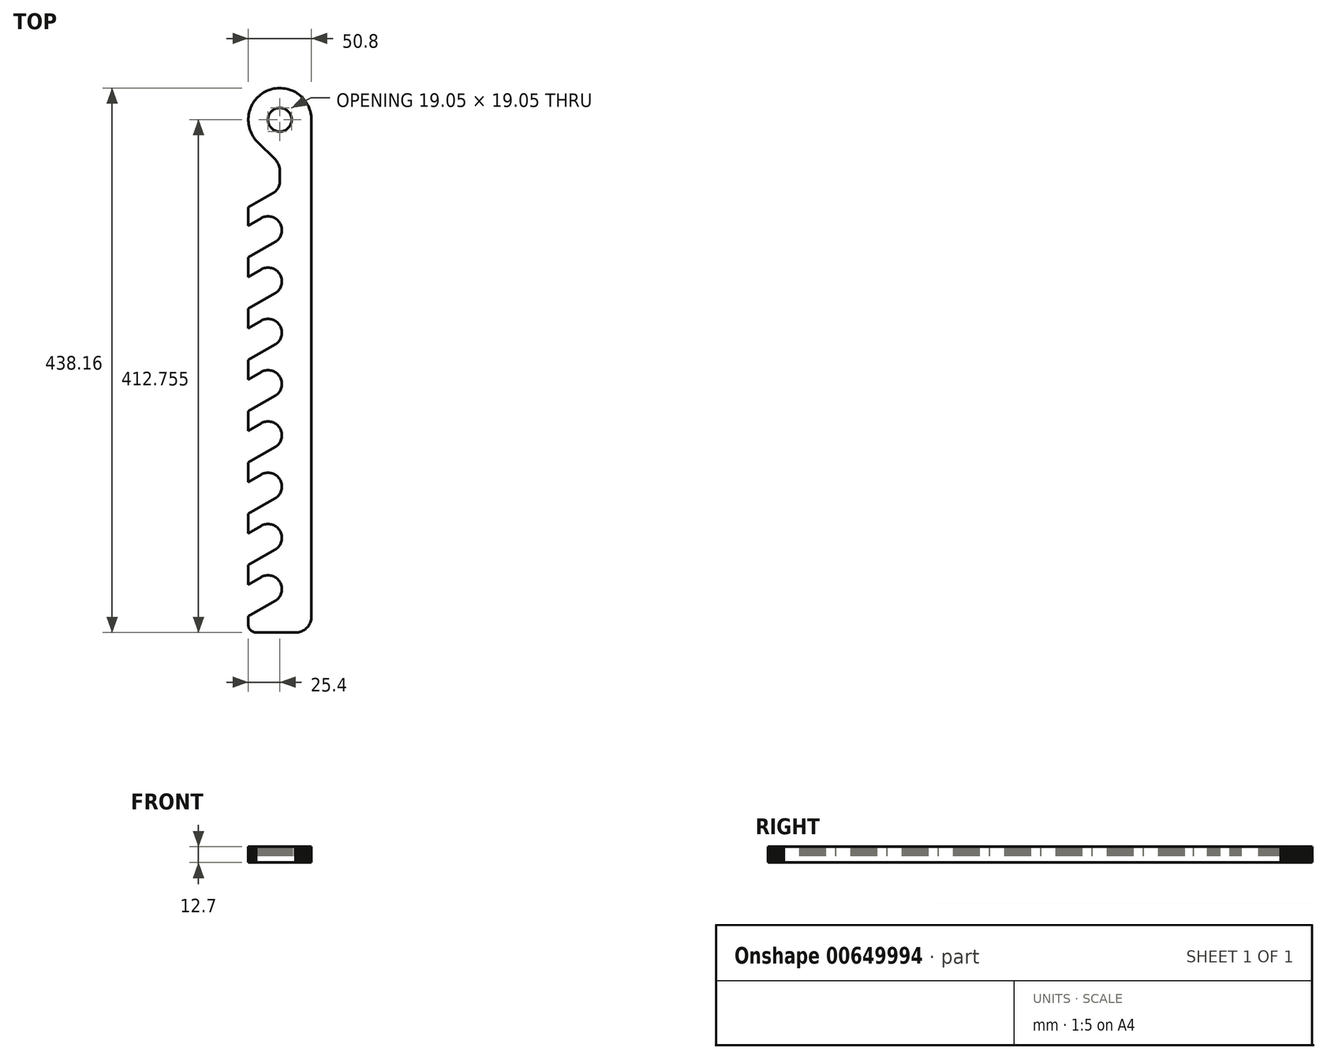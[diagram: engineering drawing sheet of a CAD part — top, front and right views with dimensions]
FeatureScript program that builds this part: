
annotation { "Feature Type Name" : "Feature", "Feature Type Description" : "" }
export const myFeature = defineFeature(function(context is Context, id is Id, definition is map)
    precondition{}
    {
        {
            var Q0;
            Q0=qCreatedBy(makeId("Top.planeOp"),FACE);
            var sketch = newSketch(context, id + "F0", { "sketchPlane" : qUnion([Q0])});
            skLineSegment(sketch, "E0", {"start": v(-25.4, -212.73) * mm, "end": v(-25.36, -213.42) * mm});
            skLineSegment(sketch, "E1", {"start": v(-25.36, -213.42) * mm, "end": v(-25.23, -214.14) * mm});
            skLineSegment(sketch, "E2", {"start": v(-25.23, -214.14) * mm, "end": v(-25.04, -214.82) * mm});
            skLineSegment(sketch, "E3", {"start": v(-25.04, -214.82) * mm, "end": v(-24.77, -215.48) * mm});
            skLineSegment(sketch, "E4", {"start": v(-24.77, -215.48) * mm, "end": v(-24.43, -216.11) * mm});
            skLineSegment(sketch, "E5", {"start": v(-24.43, -216.11) * mm, "end": v(-24.02, -216.68) * mm});
            skLineSegment(sketch, "E6", {"start": v(-24.02, -216.68) * mm, "end": v(-23.54, -217.21) * mm});
            skLineSegment(sketch, "E7", {"start": v(-23.54, -217.21) * mm, "end": v(-23, -217.68) * mm});
            skLineSegment(sketch, "E8", {"start": v(-23, -217.68) * mm, "end": v(-22.44, -218.1) * mm});
            skLineSegment(sketch, "E9", {"start": v(-22.44, -218.1) * mm, "end": v(-21.8, -218.44) * mm});
            skLineSegment(sketch, "E10", {"start": v(-21.8, -218.44) * mm, "end": v(-21.15, -218.72) * mm});
            skLineSegment(sketch, "E11", {"start": v(-21.15, -218.72) * mm, "end": v(-20.47, -218.9) * mm});
            skLineSegment(sketch, "E12", {"start": v(-20.47, -218.9) * mm, "end": v(-19.77, -219.03) * mm});
            skLineSegment(sketch, "E13", {"start": v(-19.77, -219.03) * mm, "end": v(-19.05, -219.08) * mm});
            skLineSegment(sketch, "E14", {"start": v(-19.05, -219.08) * mm, "end": v(12.7, -219.08) * mm});
            skLineSegment(sketch, "E15", {"start": v(12.7, -219.08) * mm, "end": v(13.76, -219.03) * mm});
            skLineSegment(sketch, "E16", {"start": v(13.76, -219.03) * mm, "end": v(14.8, -218.9) * mm});
            skLineSegment(sketch, "E17", {"start": v(14.8, -218.9) * mm, "end": v(15.81, -218.7) * mm});
            skLineSegment(sketch, "E18", {"start": v(15.81, -218.7) * mm, "end": v(16.83, -218.38) * mm});
            skLineSegment(sketch, "E19", {"start": v(16.83, -218.38) * mm, "end": v(17.8, -218) * mm});
            skLineSegment(sketch, "E20", {"start": v(17.8, -218) * mm, "end": v(18.75, -217.55) * mm});
            skLineSegment(sketch, "E21", {"start": v(18.75, -217.55) * mm, "end": v(19.64, -217) * mm});
            skLineSegment(sketch, "E22", {"start": v(19.64, -217) * mm, "end": v(20.51, -216.39) * mm});
            skLineSegment(sketch, "E23", {"start": v(20.51, -216.39) * mm, "end": v(21.3, -215.7) * mm});
            skLineSegment(sketch, "E24", {"start": v(21.3, -215.7) * mm, "end": v(22.03, -214.97) * mm});
            skLineSegment(sketch, "E25", {"start": v(22.03, -214.97) * mm, "end": v(22.73, -214.16) * mm});
            skLineSegment(sketch, "E26", {"start": v(22.73, -214.16) * mm, "end": v(23.33, -213.32) * mm});
            skLineSegment(sketch, "E27", {"start": v(23.33, -213.32) * mm, "end": v(23.88, -212.4) * mm});
            skLineSegment(sketch, "E28", {"start": v(23.88, -212.4) * mm, "end": v(24.32, -211.48) * mm});
            skLineSegment(sketch, "E29", {"start": v(24.32, -211.48) * mm, "end": v(24.72, -210.5) * mm});
            skLineSegment(sketch, "E30", {"start": v(24.72, -210.5) * mm, "end": v(25.02, -209.49) * mm});
            skLineSegment(sketch, "E31", {"start": v(25.02, -209.49) * mm, "end": v(25.23, -208.47) * mm});
            skLineSegment(sketch, "E32", {"start": v(25.23, -208.47) * mm, "end": v(25.36, -207.41) * mm});
            skLineSegment(sketch, "E33", {"start": v(25.36, -207.41) * mm, "end": v(25.4, -206.38) * mm});
            skLineSegment(sketch, "E34", {"start": v(0, 184.15) * mm, "end": v(0.89, 184.2) * mm});
            skLineSegment(sketch, "E35", {"start": v(0.89, 184.2) * mm, "end": v(1.76, 184.32) * mm});
            skLineSegment(sketch, "E36", {"start": v(1.76, 184.32) * mm, "end": v(2.6, 184.5) * mm});
            skLineSegment(sketch, "E37", {"start": v(2.6, 184.5) * mm, "end": v(3.45, 184.78) * mm});
            skLineSegment(sketch, "E38", {"start": v(3.45, 184.78) * mm, "end": v(4.25, 185.14) * mm});
            skLineSegment(sketch, "E39", {"start": v(4.25, 185.14) * mm, "end": v(5.02, 185.59) * mm});
            skLineSegment(sketch, "E40", {"start": v(5.02, 185.59) * mm, "end": v(5.74, 186.08) * mm});
            skLineSegment(sketch, "E41", {"start": v(5.74, 186.08) * mm, "end": v(6.41, 186.65) * mm});
            skLineSegment(sketch, "E42", {"start": v(6.41, 186.65) * mm, "end": v(7.05, 187.26) * mm});
            skLineSegment(sketch, "E43", {"start": v(7.05, 187.26) * mm, "end": v(7.6, 187.94) * mm});
            skLineSegment(sketch, "E44", {"start": v(7.6, 187.94) * mm, "end": v(8.1, 188.66) * mm});
            skLineSegment(sketch, "E45", {"start": v(8.1, 188.66) * mm, "end": v(8.53, 189.44) * mm});
            skLineSegment(sketch, "E46", {"start": v(8.53, 189.44) * mm, "end": v(8.89, 190.25) * mm});
            skLineSegment(sketch, "E47", {"start": v(8.89, 190.25) * mm, "end": v(9.17, 191.07) * mm});
            skLineSegment(sketch, "E48", {"start": v(9.17, 191.07) * mm, "end": v(9.36, 191.92) * mm});
            skLineSegment(sketch, "E49", {"start": v(9.36, 191.92) * mm, "end": v(9.48, 192.8) * mm});
            skLineSegment(sketch, "E50", {"start": v(9.48, 192.8) * mm, "end": v(9.53, 193.68) * mm});
            skLineSegment(sketch, "E51", {"start": v(9.53, 193.68) * mm, "end": v(9.48, 194.56) * mm});
            skLineSegment(sketch, "E52", {"start": v(9.48, 194.56) * mm, "end": v(9.36, 195.43) * mm});
            skLineSegment(sketch, "E53", {"start": v(9.36, 195.43) * mm, "end": v(9.17, 196.28) * mm});
            skLineSegment(sketch, "E54", {"start": v(9.17, 196.28) * mm, "end": v(8.89, 197.13) * mm});
            skLineSegment(sketch, "E55", {"start": v(8.89, 197.13) * mm, "end": v(8.53, 197.93) * mm});
            skLineSegment(sketch, "E56", {"start": v(8.53, 197.93) * mm, "end": v(8.1, 198.7) * mm});
            skLineSegment(sketch, "E57", {"start": v(8.1, 198.7) * mm, "end": v(7.6, 199.41) * mm});
            skLineSegment(sketch, "E58", {"start": v(7.6, 199.41) * mm, "end": v(7.05, 200.09) * mm});
            skLineSegment(sketch, "E59", {"start": v(7.05, 200.09) * mm, "end": v(6.41, 200.72) * mm});
            skLineSegment(sketch, "E60", {"start": v(6.41, 200.72) * mm, "end": v(5.74, 201.27) * mm});
            skLineSegment(sketch, "E61", {"start": v(5.74, 201.27) * mm, "end": v(5.02, 201.78) * mm});
            skLineSegment(sketch, "E62", {"start": v(5.02, 201.78) * mm, "end": v(4.25, 202.2) * mm});
            skLineSegment(sketch, "E63", {"start": v(4.25, 202.2) * mm, "end": v(3.45, 202.57) * mm});
            skLineSegment(sketch, "E64", {"start": v(3.45, 202.57) * mm, "end": v(2.6, 202.84) * mm});
            skLineSegment(sketch, "E65", {"start": v(2.6, 202.84) * mm, "end": v(1.76, 203.03) * mm});
            skLineSegment(sketch, "E66", {"start": v(1.76, 203.03) * mm, "end": v(0.89, 203.16) * mm});
            skLineSegment(sketch, "E67", {"start": v(0.89, 203.16) * mm, "end": v(0, 203.2) * mm});
            skLineSegment(sketch, "E68", {"start": v(0, 203.2) * mm, "end": v(-0.87, 203.16) * mm});
            skLineSegment(sketch, "E69", {"start": v(-0.87, 203.16) * mm, "end": v(-1.76, 203.03) * mm});
            skLineSegment(sketch, "E70", {"start": v(-1.76, 203.03) * mm, "end": v(-2.6, 202.84) * mm});
            skLineSegment(sketch, "E71", {"start": v(-2.6, 202.84) * mm, "end": v(-3.45, 202.57) * mm});
            skLineSegment(sketch, "E72", {"start": v(-3.45, 202.57) * mm, "end": v(-4.25, 202.2) * mm});
            skLineSegment(sketch, "E73", {"start": v(-4.25, 202.2) * mm, "end": v(-5.02, 201.78) * mm});
            skLineSegment(sketch, "E74", {"start": v(-5.02, 201.78) * mm, "end": v(-5.74, 201.27) * mm});
            skLineSegment(sketch, "E75", {"start": v(-5.74, 201.27) * mm, "end": v(-6.41, 200.72) * mm});
            skLineSegment(sketch, "E76", {"start": v(-6.41, 200.72) * mm, "end": v(-7.05, 200.09) * mm});
            skLineSegment(sketch, "E77", {"start": v(-7.05, 200.09) * mm, "end": v(-7.6, 199.41) * mm});
            skLineSegment(sketch, "E78", {"start": v(-7.6, 199.41) * mm, "end": v(-8.1, 198.7) * mm});
            skLineSegment(sketch, "E79", {"start": v(-8.1, 198.7) * mm, "end": v(-8.53, 197.93) * mm});
            skLineSegment(sketch, "E80", {"start": v(-8.53, 197.93) * mm, "end": v(-8.9, 197.13) * mm});
            skLineSegment(sketch, "E81", {"start": v(-8.9, 197.13) * mm, "end": v(-9.17, 196.28) * mm});
            skLineSegment(sketch, "E82", {"start": v(-9.17, 196.28) * mm, "end": v(-9.36, 195.43) * mm});
            skLineSegment(sketch, "E83", {"start": v(-9.36, 195.43) * mm, "end": v(-9.48, 194.56) * mm});
            skLineSegment(sketch, "E84", {"start": v(-9.48, 194.56) * mm, "end": v(-9.53, 193.68) * mm});
            skLineSegment(sketch, "E85", {"start": v(-9.53, 193.68) * mm, "end": v(-9.48, 192.8) * mm});
            skLineSegment(sketch, "E86", {"start": v(-9.48, 192.8) * mm, "end": v(-9.36, 191.92) * mm});
            skLineSegment(sketch, "E87", {"start": v(-9.36, 191.92) * mm, "end": v(-9.17, 191.07) * mm});
            skLineSegment(sketch, "E88", {"start": v(-9.17, 191.07) * mm, "end": v(-8.9, 190.25) * mm});
            skLineSegment(sketch, "E89", {"start": v(-8.9, 190.25) * mm, "end": v(-8.53, 189.44) * mm});
            skLineSegment(sketch, "E90", {"start": v(-8.53, 189.44) * mm, "end": v(-8.1, 188.66) * mm});
            skLineSegment(sketch, "E91", {"start": v(-8.1, 188.66) * mm, "end": v(-7.6, 187.94) * mm});
            skLineSegment(sketch, "E92", {"start": v(-7.6, 187.94) * mm, "end": v(-7.05, 187.26) * mm});
            skLineSegment(sketch, "E93", {"start": v(-7.05, 187.26) * mm, "end": v(-6.41, 186.65) * mm});
            skLineSegment(sketch, "E94", {"start": v(-6.41, 186.65) * mm, "end": v(-5.74, 186.08) * mm});
            skLineSegment(sketch, "E95", {"start": v(-5.74, 186.08) * mm, "end": v(-5.02, 185.59) * mm});
            skLineSegment(sketch, "E96", {"start": v(-5.02, 185.59) * mm, "end": v(-4.25, 185.14) * mm});
            skLineSegment(sketch, "E97", {"start": v(-4.25, 185.14) * mm, "end": v(-3.45, 184.78) * mm});
            skLineSegment(sketch, "E98", {"start": v(-3.45, 184.78) * mm, "end": v(-2.6, 184.5) * mm});
            skLineSegment(sketch, "E99", {"start": v(-2.6, 184.5) * mm, "end": v(-1.76, 184.32) * mm});
            skLineSegment(sketch, "E100", {"start": v(-1.76, 184.32) * mm, "end": v(-0.87, 184.2) * mm});
            skLineSegment(sketch, "E101", {"start": v(-0.87, 184.2) * mm, "end": v(0, 184.15) * mm});
            skLineSegment(sketch, "E102", {"start": v(-25.4, 123.1) * mm, "end": v(-5.55, 134.58) * mm});
            skLineSegment(sketch, "E103", {"start": v(-5.55, 134.58) * mm, "end": v(-4.74, 135.09) * mm});
            skLineSegment(sketch, "E104", {"start": v(-4.74, 135.09) * mm, "end": v(-3.98, 135.68) * mm});
            skLineSegment(sketch, "E105", {"start": v(-3.98, 135.68) * mm, "end": v(-3.26, 136.33) * mm});
            skLineSegment(sketch, "E106", {"start": v(-3.26, 136.33) * mm, "end": v(-2.6, 137.05) * mm});
            skLineSegment(sketch, "E107", {"start": v(-2.6, 137.05) * mm, "end": v(-2.01, 137.82) * mm});
            skLineSegment(sketch, "E108", {"start": v(-2.01, 137.82) * mm, "end": v(-1.48, 138.64) * mm});
            skLineSegment(sketch, "E109", {"start": v(-1.48, 138.64) * mm, "end": v(-1.04, 139.49) * mm});
            skLineSegment(sketch, "E110", {"start": v(-1.04, 139.49) * mm, "end": v(-0.68, 140.4) * mm});
            skLineSegment(sketch, "E111", {"start": v(-0.68, 140.4) * mm, "end": v(-0.38, 141.3) * mm});
            skLineSegment(sketch, "E112", {"start": v(-0.38, 141.3) * mm, "end": v(-0.17, 142.26) * mm});
            skLineSegment(sketch, "E113", {"start": v(-0.17, 142.26) * mm, "end": v(-0.04, 143.21) * mm});
            skLineSegment(sketch, "E114", {"start": v(-0.04, 143.21) * mm, "end": v(0, 144.19) * mm});
            skLineSegment(sketch, "E115", {"start": v(-3.96, 95.14) * mm, "end": v(-3.15, 95.67) * mm});
            skLineSegment(sketch, "E116", {"start": v(-3.15, 95.67) * mm, "end": v(-2.4, 96.27) * mm});
            skLineSegment(sketch, "E117", {"start": v(-2.4, 96.27) * mm, "end": v(-1.67, 96.92) * mm});
            skLineSegment(sketch, "E118", {"start": v(-1.67, 96.92) * mm, "end": v(-1.02, 97.64) * mm});
            skLineSegment(sketch, "E119", {"start": v(-1.02, 97.64) * mm, "end": v(-0.42, 98.4) * mm});
            skLineSegment(sketch, "E120", {"start": v(-0.42, 98.4) * mm, "end": v(0.1, 99.23) * mm});
            skLineSegment(sketch, "E121", {"start": v(0.1, 99.23) * mm, "end": v(0.55, 100.08) * mm});
            skLineSegment(sketch, "E122", {"start": v(0.55, 100.08) * mm, "end": v(0.91, 100.99) * mm});
            skLineSegment(sketch, "E123", {"start": v(0.91, 100.99) * mm, "end": v(1.2, 101.9) * mm});
            skLineSegment(sketch, "E124", {"start": v(1.2, 101.9) * mm, "end": v(1.42, 102.85) * mm});
            skLineSegment(sketch, "E125", {"start": v(1.42, 102.85) * mm, "end": v(1.55, 103.8) * mm});
            skLineSegment(sketch, "E126", {"start": v(1.55, 103.8) * mm, "end": v(1.59, 104.77) * mm});
            skLineSegment(sketch, "E127", {"start": v(1.59, 104.77) * mm, "end": v(1.55, 105.75) * mm});
            skLineSegment(sketch, "E128", {"start": v(1.55, 105.75) * mm, "end": v(1.42, 106.7) * mm});
            skLineSegment(sketch, "E129", {"start": v(1.42, 106.7) * mm, "end": v(1.2, 107.65) * mm});
            skLineSegment(sketch, "E130", {"start": v(1.2, 107.65) * mm, "end": v(0.91, 108.58) * mm});
            skLineSegment(sketch, "E131", {"start": v(0.91, 108.58) * mm, "end": v(0.55, 109.47) * mm});
            skLineSegment(sketch, "E132", {"start": v(0.55, 109.47) * mm, "end": v(0.1, 110.34) * mm});
            skLineSegment(sketch, "E133", {"start": v(0.1, 110.34) * mm, "end": v(-0.42, 111.15) * mm});
            skLineSegment(sketch, "E134", {"start": v(-0.42, 111.15) * mm, "end": v(-1.02, 111.93) * mm});
            skLineSegment(sketch, "E135", {"start": v(-1.02, 111.93) * mm, "end": v(-1.67, 112.63) * mm});
            skLineSegment(sketch, "E136", {"start": v(-1.67, 112.63) * mm, "end": v(-2.4, 113.28) * mm});
            skLineSegment(sketch, "E137", {"start": v(-2.4, 113.28) * mm, "end": v(-3.15, 113.88) * mm});
            skLineSegment(sketch, "E138", {"start": v(-3.15, 113.88) * mm, "end": v(-3.96, 114.4) * mm});
            skLineSegment(sketch, "E139", {"start": v(-3.96, 114.4) * mm, "end": v(-4.83, 114.85) * mm});
            skLineSegment(sketch, "E140", {"start": v(-4.83, 114.85) * mm, "end": v(-5.72, 115.21) * mm});
            skLineSegment(sketch, "E141", {"start": v(-5.72, 115.21) * mm, "end": v(-6.65, 115.5) * mm});
            skLineSegment(sketch, "E142", {"start": v(-6.65, 115.5) * mm, "end": v(-7.6, 115.72) * mm});
            skLineSegment(sketch, "E143", {"start": v(-7.6, 115.72) * mm, "end": v(-8.55, 115.85) * mm});
            skLineSegment(sketch, "E144", {"start": v(-8.55, 115.85) * mm, "end": v(-9.53, 115.89) * mm});
            skLineSegment(sketch, "E145", {"start": v(-9.53, 115.89) * mm, "end": v(-10.5, 115.85) * mm});
            skLineSegment(sketch, "E146", {"start": v(-10.5, 115.85) * mm, "end": v(-11.45, 115.72) * mm});
            skLineSegment(sketch, "E147", {"start": v(-11.45, 115.72) * mm, "end": v(-12.4, 115.5) * mm});
            skLineSegment(sketch, "E148", {"start": v(-12.4, 115.5) * mm, "end": v(-13.34, 115.21) * mm});
            skLineSegment(sketch, "E149", {"start": v(-13.34, 115.21) * mm, "end": v(-14.22, 114.85) * mm});
            skLineSegment(sketch, "E150", {"start": v(-14.22, 114.85) * mm, "end": v(-15.07, 114.4) * mm});
            skLineSegment(sketch, "E151", {"start": v(-15.07, 114.4) * mm, "end": v(-25.4, 108.44) * mm});
            skLineSegment(sketch, "E152", {"start": v(-3.96, 95.14) * mm, "end": v(-25.4, 82.78) * mm});
            skLineSegment(sketch, "E153", {"start": v(-3.96, 53.87) * mm, "end": v(-3.15, 54.4) * mm});
            skLineSegment(sketch, "E154", {"start": v(-3.15, 54.4) * mm, "end": v(-2.4, 55) * mm});
            skLineSegment(sketch, "E155", {"start": v(-2.4, 55) * mm, "end": v(-1.67, 55.65) * mm});
            skLineSegment(sketch, "E156", {"start": v(-1.67, 55.65) * mm, "end": v(-1.02, 56.37) * mm});
            skLineSegment(sketch, "E157", {"start": v(-1.02, 56.37) * mm, "end": v(-0.42, 57.13) * mm});
            skLineSegment(sketch, "E158", {"start": v(-0.42, 57.13) * mm, "end": v(0.1, 57.95) * mm});
            skLineSegment(sketch, "E159", {"start": v(0.1, 57.95) * mm, "end": v(0.55, 58.8) * mm});
            skLineSegment(sketch, "E160", {"start": v(0.55, 58.8) * mm, "end": v(0.91, 59.71) * mm});
            skLineSegment(sketch, "E161", {"start": v(0.91, 59.71) * mm, "end": v(1.2, 60.62) * mm});
            skLineSegment(sketch, "E162", {"start": v(1.2, 60.62) * mm, "end": v(1.42, 61.57) * mm});
            skLineSegment(sketch, "E163", {"start": v(1.42, 61.57) * mm, "end": v(1.55, 62.53) * mm});
            skLineSegment(sketch, "E164", {"start": v(1.55, 62.53) * mm, "end": v(1.59, 63.5) * mm});
            skLineSegment(sketch, "E165", {"start": v(1.59, 63.5) * mm, "end": v(1.55, 64.47) * mm});
            skLineSegment(sketch, "E166", {"start": v(1.55, 64.47) * mm, "end": v(1.42, 65.43) * mm});
            skLineSegment(sketch, "E167", {"start": v(1.42, 65.43) * mm, "end": v(1.2, 66.38) * mm});
            skLineSegment(sketch, "E168", {"start": v(1.2, 66.38) * mm, "end": v(0.91, 67.3) * mm});
            skLineSegment(sketch, "E169", {"start": v(0.91, 67.3) * mm, "end": v(0.55, 68.2) * mm});
            skLineSegment(sketch, "E170", {"start": v(0.55, 68.2) * mm, "end": v(0.1, 69.07) * mm});
            skLineSegment(sketch, "E171", {"start": v(0.1, 69.07) * mm, "end": v(-0.42, 69.87) * mm});
            skLineSegment(sketch, "E172", {"start": v(-0.42, 69.87) * mm, "end": v(-1.02, 70.65) * mm});
            skLineSegment(sketch, "E173", {"start": v(-1.02, 70.65) * mm, "end": v(-1.67, 71.35) * mm});
            skLineSegment(sketch, "E174", {"start": v(-1.67, 71.35) * mm, "end": v(-2.4, 72) * mm});
            skLineSegment(sketch, "E175", {"start": v(-2.4, 72) * mm, "end": v(-3.15, 72.6) * mm});
            skLineSegment(sketch, "E176", {"start": v(-3.15, 72.6) * mm, "end": v(-3.96, 73.13) * mm});
            skLineSegment(sketch, "E177", {"start": v(-3.96, 73.13) * mm, "end": v(-4.83, 73.58) * mm});
            skLineSegment(sketch, "E178", {"start": v(-4.83, 73.58) * mm, "end": v(-5.72, 73.94) * mm});
            skLineSegment(sketch, "E179", {"start": v(-5.72, 73.94) * mm, "end": v(-6.65, 74.23) * mm});
            skLineSegment(sketch, "E180", {"start": v(-6.65, 74.23) * mm, "end": v(-7.6, 74.44) * mm});
            skLineSegment(sketch, "E181", {"start": v(-7.6, 74.44) * mm, "end": v(-8.55, 74.57) * mm});
            skLineSegment(sketch, "E182", {"start": v(-8.55, 74.57) * mm, "end": v(-9.53, 74.61) * mm});
            skLineSegment(sketch, "E183", {"start": v(-9.53, 74.61) * mm, "end": v(-10.5, 74.57) * mm});
            skLineSegment(sketch, "E184", {"start": v(-10.5, 74.57) * mm, "end": v(-11.45, 74.44) * mm});
            skLineSegment(sketch, "E185", {"start": v(-11.45, 74.44) * mm, "end": v(-12.4, 74.23) * mm});
            skLineSegment(sketch, "E186", {"start": v(-12.4, 74.23) * mm, "end": v(-13.34, 73.94) * mm});
            skLineSegment(sketch, "E187", {"start": v(-13.34, 73.94) * mm, "end": v(-14.22, 73.58) * mm});
            skLineSegment(sketch, "E188", {"start": v(-14.22, 73.58) * mm, "end": v(-15.07, 73.13) * mm});
            skLineSegment(sketch, "E189", {"start": v(-15.07, 73.13) * mm, "end": v(-25.4, 67.16) * mm});
            skLineSegment(sketch, "E190", {"start": v(-3.96, 53.87) * mm, "end": v(-25.4, 41.5) * mm});
            skLineSegment(sketch, "E191", {"start": v(-3.96, 12.6) * mm, "end": v(-3.15, 13.12) * mm});
            skLineSegment(sketch, "E192", {"start": v(-3.15, 13.12) * mm, "end": v(-2.4, 13.72) * mm});
            skLineSegment(sketch, "E193", {"start": v(-2.4, 13.72) * mm, "end": v(-1.67, 14.37) * mm});
            skLineSegment(sketch, "E194", {"start": v(-1.67, 14.37) * mm, "end": v(-1.02, 15.1) * mm});
            skLineSegment(sketch, "E195", {"start": v(-1.02, 15.1) * mm, "end": v(-0.42, 15.85) * mm});
            skLineSegment(sketch, "E196", {"start": v(-0.42, 15.85) * mm, "end": v(0.1, 16.68) * mm});
            skLineSegment(sketch, "E197", {"start": v(0.1, 16.68) * mm, "end": v(0.55, 17.53) * mm});
            skLineSegment(sketch, "E198", {"start": v(0.55, 17.53) * mm, "end": v(0.91, 18.44) * mm});
            skLineSegment(sketch, "E199", {"start": v(0.91, 18.44) * mm, "end": v(1.2, 19.35) * mm});
            skLineSegment(sketch, "E200", {"start": v(1.2, 19.35) * mm, "end": v(1.42, 20.3) * mm});
            skLineSegment(sketch, "E201", {"start": v(1.42, 20.3) * mm, "end": v(1.55, 21.25) * mm});
            skLineSegment(sketch, "E202", {"start": v(1.55, 21.25) * mm, "end": v(1.59, 22.22) * mm});
            skLineSegment(sketch, "E203", {"start": v(1.59, 22.22) * mm, "end": v(1.55, 23.2) * mm});
            skLineSegment(sketch, "E204", {"start": v(1.55, 23.2) * mm, "end": v(1.42, 24.15) * mm});
            skLineSegment(sketch, "E205", {"start": v(1.42, 24.15) * mm, "end": v(1.2, 25.1) * mm});
            skLineSegment(sketch, "E206", {"start": v(1.2, 25.1) * mm, "end": v(0.91, 26.03) * mm});
            skLineSegment(sketch, "E207", {"start": v(0.91, 26.03) * mm, "end": v(0.55, 26.92) * mm});
            skLineSegment(sketch, "E208", {"start": v(0.55, 26.92) * mm, "end": v(0.1, 27.8) * mm});
            skLineSegment(sketch, "E209", {"start": v(0.1, 27.8) * mm, "end": v(-0.42, 28.6) * mm});
            skLineSegment(sketch, "E210", {"start": v(-0.42, 28.6) * mm, "end": v(-1.02, 29.38) * mm});
            skLineSegment(sketch, "E211", {"start": v(-1.02, 29.38) * mm, "end": v(-1.67, 30.08) * mm});
            skLineSegment(sketch, "E212", {"start": v(-1.67, 30.08) * mm, "end": v(-2.4, 30.73) * mm});
            skLineSegment(sketch, "E213", {"start": v(-2.4, 30.73) * mm, "end": v(-3.15, 31.33) * mm});
            skLineSegment(sketch, "E214", {"start": v(-3.15, 31.33) * mm, "end": v(-3.96, 31.86) * mm});
            skLineSegment(sketch, "E215", {"start": v(-3.96, 31.86) * mm, "end": v(-4.83, 32.3) * mm});
            skLineSegment(sketch, "E216", {"start": v(-4.83, 32.3) * mm, "end": v(-5.72, 32.66) * mm});
            skLineSegment(sketch, "E217", {"start": v(-5.72, 32.66) * mm, "end": v(-6.65, 32.96) * mm});
            skLineSegment(sketch, "E218", {"start": v(-6.65, 32.96) * mm, "end": v(-7.6, 33.17) * mm});
            skLineSegment(sketch, "E219", {"start": v(-7.6, 33.17) * mm, "end": v(-8.55, 33.3) * mm});
            skLineSegment(sketch, "E220", {"start": v(-8.55, 33.3) * mm, "end": v(-9.53, 33.34) * mm});
            skLineSegment(sketch, "E221", {"start": v(-9.53, 33.34) * mm, "end": v(-10.5, 33.3) * mm});
            skLineSegment(sketch, "E222", {"start": v(-10.5, 33.3) * mm, "end": v(-11.45, 33.17) * mm});
            skLineSegment(sketch, "E223", {"start": v(-11.45, 33.17) * mm, "end": v(-12.4, 32.96) * mm});
            skLineSegment(sketch, "E224", {"start": v(-12.4, 32.96) * mm, "end": v(-13.34, 32.66) * mm});
            skLineSegment(sketch, "E225", {"start": v(-13.34, 32.66) * mm, "end": v(-14.22, 32.3) * mm});
            skLineSegment(sketch, "E226", {"start": v(-14.22, 32.3) * mm, "end": v(-15.07, 31.86) * mm});
            skLineSegment(sketch, "E227", {"start": v(-15.07, 31.86) * mm, "end": v(-25.4, 25.89) * mm});
            skLineSegment(sketch, "E228", {"start": v(-3.96, 12.6) * mm, "end": v(-25.4, 0.23) * mm});
            skLineSegment(sketch, "E229", {"start": v(-3.96, -28.68) * mm, "end": v(-3.15, -28.15) * mm});
            skLineSegment(sketch, "E230", {"start": v(-3.15, -28.15) * mm, "end": v(-2.4, -27.56) * mm});
            skLineSegment(sketch, "E231", {"start": v(-2.4, -27.56) * mm, "end": v(-1.67, -26.9) * mm});
            skLineSegment(sketch, "E232", {"start": v(-1.67, -26.9) * mm, "end": v(-1.02, -26.18) * mm});
            skLineSegment(sketch, "E233", {"start": v(-1.02, -26.18) * mm, "end": v(-0.42, -25.42) * mm});
            skLineSegment(sketch, "E234", {"start": v(-0.42, -25.42) * mm, "end": v(0.1, -24.6) * mm});
            skLineSegment(sketch, "E235", {"start": v(0.1, -24.6) * mm, "end": v(0.55, -23.75) * mm});
            skLineSegment(sketch, "E236", {"start": v(0.55, -23.75) * mm, "end": v(0.91, -22.84) * mm});
            skLineSegment(sketch, "E237", {"start": v(0.91, -22.84) * mm, "end": v(1.2, -21.93) * mm});
            skLineSegment(sketch, "E238", {"start": v(1.2, -21.93) * mm, "end": v(1.42, -20.98) * mm});
            skLineSegment(sketch, "E239", {"start": v(1.42, -20.98) * mm, "end": v(1.55, -20.02) * mm});
            skLineSegment(sketch, "E240", {"start": v(1.55, -20.02) * mm, "end": v(1.59, -19.05) * mm});
            skLineSegment(sketch, "E241", {"start": v(1.59, -19.05) * mm, "end": v(1.55, -18.08) * mm});
            skLineSegment(sketch, "E242", {"start": v(1.55, -18.08) * mm, "end": v(1.42, -17.12) * mm});
            skLineSegment(sketch, "E243", {"start": v(1.42, -17.12) * mm, "end": v(1.2, -16.17) * mm});
            skLineSegment(sketch, "E244", {"start": v(1.2, -16.17) * mm, "end": v(0.91, -15.24) * mm});
            skLineSegment(sketch, "E245", {"start": v(0.91, -15.24) * mm, "end": v(0.55, -14.35) * mm});
            skLineSegment(sketch, "E246", {"start": v(0.55, -14.35) * mm, "end": v(0.1, -13.48) * mm});
            skLineSegment(sketch, "E247", {"start": v(0.1, -13.48) * mm, "end": v(-0.42, -12.68) * mm});
            skLineSegment(sketch, "E248", {"start": v(-0.42, -12.68) * mm, "end": v(-1.02, -11.9) * mm});
            skLineSegment(sketch, "E249", {"start": v(-1.02, -11.9) * mm, "end": v(-1.67, -11.2) * mm});
            skLineSegment(sketch, "E250", {"start": v(-1.67, -11.2) * mm, "end": v(-2.4, -10.54) * mm});
            skLineSegment(sketch, "E251", {"start": v(-2.4, -10.54) * mm, "end": v(-3.15, -9.95) * mm});
            skLineSegment(sketch, "E252", {"start": v(-3.15, -9.95) * mm, "end": v(-3.96, -9.42) * mm});
            skLineSegment(sketch, "E253", {"start": v(-3.96, -9.42) * mm, "end": v(-4.83, -8.97) * mm});
            skLineSegment(sketch, "E254", {"start": v(-4.83, -8.97) * mm, "end": v(-5.72, -8.61) * mm});
            skLineSegment(sketch, "E255", {"start": v(-5.72, -8.61) * mm, "end": v(-6.65, -8.32) * mm});
            skLineSegment(sketch, "E256", {"start": v(-6.65, -8.32) * mm, "end": v(-7.6, -8.1) * mm});
            skLineSegment(sketch, "E257", {"start": v(-7.6, -8.1) * mm, "end": v(-8.55, -7.98) * mm});
            skLineSegment(sketch, "E258", {"start": v(-8.55, -7.98) * mm, "end": v(-9.53, -7.94) * mm});
            skLineSegment(sketch, "E259", {"start": v(-9.53, -7.94) * mm, "end": v(-10.5, -7.98) * mm});
            skLineSegment(sketch, "E260", {"start": v(-10.5, -7.98) * mm, "end": v(-11.45, -8.1) * mm});
            skLineSegment(sketch, "E261", {"start": v(-11.45, -8.1) * mm, "end": v(-12.4, -8.32) * mm});
            skLineSegment(sketch, "E262", {"start": v(-12.4, -8.32) * mm, "end": v(-13.34, -8.61) * mm});
            skLineSegment(sketch, "E263", {"start": v(-13.34, -8.61) * mm, "end": v(-14.22, -8.97) * mm});
            skLineSegment(sketch, "E264", {"start": v(-14.22, -8.97) * mm, "end": v(-15.07, -9.42) * mm});
            skLineSegment(sketch, "E265", {"start": v(-15.07, -9.42) * mm, "end": v(-25.4, -15.39) * mm});
            skLineSegment(sketch, "E266", {"start": v(-3.96, -28.68) * mm, "end": v(-25.4, -41.04) * mm});
            skLineSegment(sketch, "E267", {"start": v(-3.96, -69.96) * mm, "end": v(-3.15, -69.43) * mm});
            skLineSegment(sketch, "E268", {"start": v(-3.15, -69.43) * mm, "end": v(-2.4, -68.83) * mm});
            skLineSegment(sketch, "E269", {"start": v(-2.4, -68.83) * mm, "end": v(-1.67, -68.18) * mm});
            skLineSegment(sketch, "E270", {"start": v(-1.67, -68.18) * mm, "end": v(-1.02, -67.46) * mm});
            skLineSegment(sketch, "E271", {"start": v(-1.02, -67.46) * mm, "end": v(-0.42, -66.7) * mm});
            skLineSegment(sketch, "E272", {"start": v(-0.42, -66.7) * mm, "end": v(0.1, -65.87) * mm});
            skLineSegment(sketch, "E273", {"start": v(0.1, -65.87) * mm, "end": v(0.55, -65.02) * mm});
            skLineSegment(sketch, "E274", {"start": v(0.55, -65.02) * mm, "end": v(0.91, -64.11) * mm});
            skLineSegment(sketch, "E275", {"start": v(0.91, -64.11) * mm, "end": v(1.2, -63.2) * mm});
            skLineSegment(sketch, "E276", {"start": v(1.2, -63.2) * mm, "end": v(1.42, -62.25) * mm});
            skLineSegment(sketch, "E277", {"start": v(1.42, -62.25) * mm, "end": v(1.55, -61.3) * mm});
            skLineSegment(sketch, "E278", {"start": v(1.55, -61.3) * mm, "end": v(1.59, -60.33) * mm});
            skLineSegment(sketch, "E279", {"start": v(1.59, -60.33) * mm, "end": v(1.55, -59.35) * mm});
            skLineSegment(sketch, "E280", {"start": v(1.55, -59.35) * mm, "end": v(1.42, -58.4) * mm});
            skLineSegment(sketch, "E281", {"start": v(1.42, -58.4) * mm, "end": v(1.2, -57.45) * mm});
            skLineSegment(sketch, "E282", {"start": v(1.2, -57.45) * mm, "end": v(0.91, -56.52) * mm});
            skLineSegment(sketch, "E283", {"start": v(0.91, -56.52) * mm, "end": v(0.55, -55.63) * mm});
            skLineSegment(sketch, "E284", {"start": v(0.55, -55.63) * mm, "end": v(0.1, -54.76) * mm});
            skLineSegment(sketch, "E285", {"start": v(0.1, -54.76) * mm, "end": v(-0.42, -53.95) * mm});
            skLineSegment(sketch, "E286", {"start": v(-0.42, -53.95) * mm, "end": v(-1.02, -53.17) * mm});
            skLineSegment(sketch, "E287", {"start": v(-1.02, -53.17) * mm, "end": v(-1.67, -52.47) * mm});
            skLineSegment(sketch, "E288", {"start": v(-1.67, -52.47) * mm, "end": v(-2.4, -51.82) * mm});
            skLineSegment(sketch, "E289", {"start": v(-2.4, -51.82) * mm, "end": v(-3.15, -51.22) * mm});
            skLineSegment(sketch, "E290", {"start": v(-3.15, -51.22) * mm, "end": v(-3.96, -50.7) * mm});
            skLineSegment(sketch, "E291", {"start": v(-3.96, -50.7) * mm, "end": v(-4.83, -50.25) * mm});
            skLineSegment(sketch, "E292", {"start": v(-4.83, -50.25) * mm, "end": v(-5.72, -49.89) * mm});
            skLineSegment(sketch, "E293", {"start": v(-5.72, -49.89) * mm, "end": v(-6.65, -49.6) * mm});
            skLineSegment(sketch, "E294", {"start": v(-6.65, -49.6) * mm, "end": v(-7.6, -49.38) * mm});
            skLineSegment(sketch, "E295", {"start": v(-7.6, -49.38) * mm, "end": v(-8.55, -49.25) * mm});
            skLineSegment(sketch, "E296", {"start": v(-8.55, -49.25) * mm, "end": v(-9.53, -49.21) * mm});
            skLineSegment(sketch, "E297", {"start": v(-9.53, -49.21) * mm, "end": v(-10.5, -49.25) * mm});
            skLineSegment(sketch, "E298", {"start": v(-10.5, -49.25) * mm, "end": v(-11.45, -49.38) * mm});
            skLineSegment(sketch, "E299", {"start": v(-11.45, -49.38) * mm, "end": v(-12.4, -49.6) * mm});
            skLineSegment(sketch, "E300", {"start": v(-12.4, -49.6) * mm, "end": v(-13.34, -49.89) * mm});
            skLineSegment(sketch, "E301", {"start": v(-13.34, -49.89) * mm, "end": v(-14.22, -50.25) * mm});
            skLineSegment(sketch, "E302", {"start": v(-14.22, -50.25) * mm, "end": v(-15.07, -50.7) * mm});
            skLineSegment(sketch, "E303", {"start": v(-15.07, -50.7) * mm, "end": v(-25.4, -56.66) * mm});
            skLineSegment(sketch, "E304", {"start": v(-3.96, -69.96) * mm, "end": v(-25.4, -82.32) * mm});
            skLineSegment(sketch, "E305", {"start": v(-3.96, -111.23) * mm, "end": v(-3.15, -110.7) * mm});
            skLineSegment(sketch, "E306", {"start": v(-3.15, -110.7) * mm, "end": v(-2.4, -110.1) * mm});
            skLineSegment(sketch, "E307", {"start": v(-2.4, -110.1) * mm, "end": v(-1.67, -109.45) * mm});
            skLineSegment(sketch, "E308", {"start": v(-1.67, -109.45) * mm, "end": v(-1.02, -108.73) * mm});
            skLineSegment(sketch, "E309", {"start": v(-1.02, -108.73) * mm, "end": v(-0.42, -107.97) * mm});
            skLineSegment(sketch, "E310", {"start": v(-0.42, -107.97) * mm, "end": v(0.1, -107.15) * mm});
            skLineSegment(sketch, "E311", {"start": v(0.1, -107.15) * mm, "end": v(0.55, -106.3) * mm});
            skLineSegment(sketch, "E312", {"start": v(0.55, -106.3) * mm, "end": v(0.91, -105.39) * mm});
            skLineSegment(sketch, "E313", {"start": v(0.91, -105.39) * mm, "end": v(1.2, -104.48) * mm});
            skLineSegment(sketch, "E314", {"start": v(1.2, -104.48) * mm, "end": v(1.42, -103.53) * mm});
            skLineSegment(sketch, "E315", {"start": v(1.42, -103.53) * mm, "end": v(1.55, -102.57) * mm});
            skLineSegment(sketch, "E316", {"start": v(1.55, -102.57) * mm, "end": v(1.59, -101.6) * mm});
            skLineSegment(sketch, "E317", {"start": v(1.59, -101.6) * mm, "end": v(1.55, -100.63) * mm});
            skLineSegment(sketch, "E318", {"start": v(1.55, -100.63) * mm, "end": v(1.42, -99.67) * mm});
            skLineSegment(sketch, "E319", {"start": v(1.42, -99.67) * mm, "end": v(1.2, -98.72) * mm});
            skLineSegment(sketch, "E320", {"start": v(1.2, -98.72) * mm, "end": v(0.91, -97.8) * mm});
            skLineSegment(sketch, "E321", {"start": v(0.91, -97.8) * mm, "end": v(0.55, -96.9) * mm});
            skLineSegment(sketch, "E322", {"start": v(0.55, -96.9) * mm, "end": v(0.1, -96.03) * mm});
            skLineSegment(sketch, "E323", {"start": v(0.1, -96.03) * mm, "end": v(-0.42, -95.23) * mm});
            skLineSegment(sketch, "E324", {"start": v(-0.42, -95.23) * mm, "end": v(-1.02, -94.45) * mm});
            skLineSegment(sketch, "E325", {"start": v(-1.02, -94.45) * mm, "end": v(-1.67, -93.75) * mm});
            skLineSegment(sketch, "E326", {"start": v(-1.67, -93.75) * mm, "end": v(-2.4, -93.1) * mm});
            skLineSegment(sketch, "E327", {"start": v(-2.4, -93.1) * mm, "end": v(-3.15, -92.5) * mm});
            skLineSegment(sketch, "E328", {"start": v(-3.15, -92.5) * mm, "end": v(-3.96, -91.97) * mm});
            skLineSegment(sketch, "E329", {"start": v(-3.96, -91.97) * mm, "end": v(-4.83, -91.52) * mm});
            skLineSegment(sketch, "E330", {"start": v(-4.83, -91.52) * mm, "end": v(-5.72, -91.16) * mm});
            skLineSegment(sketch, "E331", {"start": v(-5.72, -91.16) * mm, "end": v(-6.65, -90.87) * mm});
            skLineSegment(sketch, "E332", {"start": v(-6.65, -90.87) * mm, "end": v(-7.6, -90.66) * mm});
            skLineSegment(sketch, "E333", {"start": v(-7.6, -90.66) * mm, "end": v(-8.55, -90.53) * mm});
            skLineSegment(sketch, "E334", {"start": v(-8.55, -90.53) * mm, "end": v(-9.53, -90.49) * mm});
            skLineSegment(sketch, "E335", {"start": v(-9.53, -90.49) * mm, "end": v(-10.5, -90.53) * mm});
            skLineSegment(sketch, "E336", {"start": v(-10.5, -90.53) * mm, "end": v(-11.45, -90.66) * mm});
            skLineSegment(sketch, "E337", {"start": v(-11.45, -90.66) * mm, "end": v(-12.4, -90.87) * mm});
            skLineSegment(sketch, "E338", {"start": v(-12.4, -90.87) * mm, "end": v(-13.34, -91.16) * mm});
            skLineSegment(sketch, "E339", {"start": v(-13.34, -91.16) * mm, "end": v(-14.22, -91.52) * mm});
            skLineSegment(sketch, "E340", {"start": v(-14.22, -91.52) * mm, "end": v(-15.07, -91.97) * mm});
            skLineSegment(sketch, "E341", {"start": v(-15.07, -91.97) * mm, "end": v(-25.4, -97.94) * mm});
            skLineSegment(sketch, "E342", {"start": v(-3.96, -111.23) * mm, "end": v(-25.4, -123.6) * mm});
            skLineSegment(sketch, "E343", {"start": v(-3.96, -152.5) * mm, "end": v(-3.15, -151.98) * mm});
            skLineSegment(sketch, "E344", {"start": v(-3.15, -151.98) * mm, "end": v(-2.4, -151.38) * mm});
            skLineSegment(sketch, "E345", {"start": v(-2.4, -151.38) * mm, "end": v(-1.67, -150.73) * mm});
            skLineSegment(sketch, "E346", {"start": v(-1.67, -150.73) * mm, "end": v(-1.02, -150) * mm});
            skLineSegment(sketch, "E347", {"start": v(-1.02, -150) * mm, "end": v(-0.42, -149.25) * mm});
            skLineSegment(sketch, "E348", {"start": v(-0.42, -149.25) * mm, "end": v(0.1, -148.42) * mm});
            skLineSegment(sketch, "E349", {"start": v(0.1, -148.42) * mm, "end": v(0.55, -147.57) * mm});
            skLineSegment(sketch, "E350", {"start": v(0.55, -147.57) * mm, "end": v(0.91, -146.66) * mm});
            skLineSegment(sketch, "E351", {"start": v(0.91, -146.66) * mm, "end": v(1.2, -145.75) * mm});
            skLineSegment(sketch, "E352", {"start": v(1.2, -145.75) * mm, "end": v(1.42, -144.8) * mm});
            skLineSegment(sketch, "E353", {"start": v(1.42, -144.8) * mm, "end": v(1.55, -143.85) * mm});
            skLineSegment(sketch, "E354", {"start": v(1.55, -143.85) * mm, "end": v(1.59, -142.88) * mm});
            skLineSegment(sketch, "E355", {"start": v(1.59, -142.88) * mm, "end": v(1.55, -141.9) * mm});
            skLineSegment(sketch, "E356", {"start": v(1.55, -141.9) * mm, "end": v(1.42, -140.95) * mm});
            skLineSegment(sketch, "E357", {"start": v(1.42, -140.95) * mm, "end": v(1.2, -140) * mm});
            skLineSegment(sketch, "E358", {"start": v(1.2, -140) * mm, "end": v(0.91, -139.07) * mm});
            skLineSegment(sketch, "E359", {"start": v(0.91, -139.07) * mm, "end": v(0.55, -138.18) * mm});
            skLineSegment(sketch, "E360", {"start": v(0.55, -138.18) * mm, "end": v(0.1, -137.3) * mm});
            skLineSegment(sketch, "E361", {"start": v(0.1, -137.3) * mm, "end": v(-0.42, -136.5) * mm});
            skLineSegment(sketch, "E362", {"start": v(-0.42, -136.5) * mm, "end": v(-1.02, -135.72) * mm});
            skLineSegment(sketch, "E363", {"start": v(-1.02, -135.72) * mm, "end": v(-1.67, -135.02) * mm});
            skLineSegment(sketch, "E364", {"start": v(-1.67, -135.02) * mm, "end": v(-2.4, -134.37) * mm});
            skLineSegment(sketch, "E365", {"start": v(-2.4, -134.37) * mm, "end": v(-3.15, -133.77) * mm});
            skLineSegment(sketch, "E366", {"start": v(-3.15, -133.77) * mm, "end": v(-3.96, -133.24) * mm});
            skLineSegment(sketch, "E367", {"start": v(-3.96, -133.24) * mm, "end": v(-4.83, -132.8) * mm});
            skLineSegment(sketch, "E368", {"start": v(-4.83, -132.8) * mm, "end": v(-5.72, -132.44) * mm});
            skLineSegment(sketch, "E369", {"start": v(-5.72, -132.44) * mm, "end": v(-6.65, -132.14) * mm});
            skLineSegment(sketch, "E370", {"start": v(-6.65, -132.14) * mm, "end": v(-7.6, -131.93) * mm});
            skLineSegment(sketch, "E371", {"start": v(-7.6, -131.93) * mm, "end": v(-8.55, -131.8) * mm});
            skLineSegment(sketch, "E372", {"start": v(-8.55, -131.8) * mm, "end": v(-9.53, -131.76) * mm});
            skLineSegment(sketch, "E373", {"start": v(-9.53, -131.76) * mm, "end": v(-10.5, -131.8) * mm});
            skLineSegment(sketch, "E374", {"start": v(-10.5, -131.8) * mm, "end": v(-11.45, -131.93) * mm});
            skLineSegment(sketch, "E375", {"start": v(-11.45, -131.93) * mm, "end": v(-12.4, -132.14) * mm});
            skLineSegment(sketch, "E376", {"start": v(-12.4, -132.14) * mm, "end": v(-13.34, -132.44) * mm});
            skLineSegment(sketch, "E377", {"start": v(-13.34, -132.44) * mm, "end": v(-14.22, -132.8) * mm});
            skLineSegment(sketch, "E378", {"start": v(-14.22, -132.8) * mm, "end": v(-15.07, -133.24) * mm});
            skLineSegment(sketch, "E379", {"start": v(-15.07, -133.24) * mm, "end": v(-25.4, -139.21) * mm});
            skLineSegment(sketch, "E380", {"start": v(-3.96, -152.5) * mm, "end": v(-25.4, -164.87) * mm});
            skLineSegment(sketch, "E381", {"start": v(-25.4, -212.73) * mm, "end": v(-25.4, -211.65) * mm});
            skLineSegment(sketch, "E382", {"start": v(-3.96, -193.78) * mm, "end": v(-3.15, -193.25) * mm});
            skLineSegment(sketch, "E383", {"start": v(-3.15, -193.25) * mm, "end": v(-2.4, -192.66) * mm});
            skLineSegment(sketch, "E384", {"start": v(-2.4, -192.66) * mm, "end": v(-1.67, -192) * mm});
            skLineSegment(sketch, "E385", {"start": v(-1.67, -192) * mm, "end": v(-1.02, -191.28) * mm});
            skLineSegment(sketch, "E386", {"start": v(-1.02, -191.28) * mm, "end": v(-0.42, -190.52) * mm});
            skLineSegment(sketch, "E387", {"start": v(-0.42, -190.52) * mm, "end": v(0.1, -189.7) * mm});
            skLineSegment(sketch, "E388", {"start": v(0.1, -189.7) * mm, "end": v(0.55, -188.85) * mm});
            skLineSegment(sketch, "E389", {"start": v(0.55, -188.85) * mm, "end": v(0.91, -187.94) * mm});
            skLineSegment(sketch, "E390", {"start": v(0.91, -187.94) * mm, "end": v(1.2, -187.03) * mm});
            skLineSegment(sketch, "E391", {"start": v(1.2, -187.03) * mm, "end": v(1.42, -186.08) * mm});
            skLineSegment(sketch, "E392", {"start": v(1.42, -186.08) * mm, "end": v(1.55, -185.12) * mm});
            skLineSegment(sketch, "E393", {"start": v(1.55, -185.12) * mm, "end": v(1.59, -184.15) * mm});
            skLineSegment(sketch, "E394", {"start": v(1.59, -184.15) * mm, "end": v(1.55, -183.18) * mm});
            skLineSegment(sketch, "E395", {"start": v(1.55, -183.18) * mm, "end": v(1.42, -182.22) * mm});
            skLineSegment(sketch, "E396", {"start": v(1.42, -182.22) * mm, "end": v(1.2, -181.27) * mm});
            skLineSegment(sketch, "E397", {"start": v(1.2, -181.27) * mm, "end": v(0.91, -180.34) * mm});
            skLineSegment(sketch, "E398", {"start": v(0.91, -180.34) * mm, "end": v(0.55, -179.45) * mm});
            skLineSegment(sketch, "E399", {"start": v(0.55, -179.45) * mm, "end": v(0.1, -178.58) * mm});
            skLineSegment(sketch, "E400", {"start": v(0.1, -178.58) * mm, "end": v(-0.42, -177.78) * mm});
            skLineSegment(sketch, "E401", {"start": v(-0.42, -177.78) * mm, "end": v(-1.02, -177) * mm});
            skLineSegment(sketch, "E402", {"start": v(-1.02, -177) * mm, "end": v(-1.67, -176.3) * mm});
            skLineSegment(sketch, "E403", {"start": v(-1.67, -176.3) * mm, "end": v(-2.4, -175.64) * mm});
            skLineSegment(sketch, "E404", {"start": v(-2.4, -175.64) * mm, "end": v(-3.15, -175.05) * mm});
            skLineSegment(sketch, "E405", {"start": v(-3.15, -175.05) * mm, "end": v(-3.96, -174.52) * mm});
            skLineSegment(sketch, "E406", {"start": v(-3.96, -174.52) * mm, "end": v(-4.83, -174.07) * mm});
            skLineSegment(sketch, "E407", {"start": v(-4.83, -174.07) * mm, "end": v(-5.72, -173.71) * mm});
            skLineSegment(sketch, "E408", {"start": v(-5.72, -173.71) * mm, "end": v(-6.65, -173.42) * mm});
            skLineSegment(sketch, "E409", {"start": v(-6.65, -173.42) * mm, "end": v(-7.6, -173.2) * mm});
            skLineSegment(sketch, "E410", {"start": v(-7.6, -173.2) * mm, "end": v(-8.55, -173.08) * mm});
            skLineSegment(sketch, "E411", {"start": v(-8.55, -173.08) * mm, "end": v(-9.53, -173.04) * mm});
            skLineSegment(sketch, "E412", {"start": v(-9.53, -173.04) * mm, "end": v(-10.5, -173.08) * mm});
            skLineSegment(sketch, "E413", {"start": v(-10.5, -173.08) * mm, "end": v(-11.45, -173.2) * mm});
            skLineSegment(sketch, "E414", {"start": v(-11.45, -173.2) * mm, "end": v(-12.4, -173.42) * mm});
            skLineSegment(sketch, "E415", {"start": v(-12.4, -173.42) * mm, "end": v(-13.34, -173.71) * mm});
            skLineSegment(sketch, "E416", {"start": v(-13.34, -173.71) * mm, "end": v(-14.22, -174.07) * mm});
            skLineSegment(sketch, "E417", {"start": v(-14.22, -174.07) * mm, "end": v(-15.07, -174.52) * mm});
            skLineSegment(sketch, "E418", {"start": v(-15.07, -174.52) * mm, "end": v(-25.4, -180.49) * mm});
            skLineSegment(sketch, "E419", {"start": v(-3.96, -193.78) * mm, "end": v(-25.4, -206.14) * mm});
            skLineSegment(sketch, "E420", {"start": v(25.4, -206.38) * mm, "end": v(25.4, 193.68) * mm});
            skLineSegment(sketch, "E421", {"start": v(25.4, 193.68) * mm, "end": v(25.36, 195.16) * mm});
            skLineSegment(sketch, "E422", {"start": v(25.36, 195.16) * mm, "end": v(25.23, 196.64) * mm});
            skLineSegment(sketch, "E423", {"start": v(25.23, 196.64) * mm, "end": v(25.02, 198.12) * mm});
            skLineSegment(sketch, "E424", {"start": v(25.02, 198.12) * mm, "end": v(24.7, 199.58) * mm});
            skLineSegment(sketch, "E425", {"start": v(24.7, 199.58) * mm, "end": v(24.32, 201.02) * mm});
            skLineSegment(sketch, "E426", {"start": v(24.32, 201.02) * mm, "end": v(23.85, 202.42) * mm});
            skLineSegment(sketch, "E427", {"start": v(23.85, 202.42) * mm, "end": v(23.28, 203.81) * mm});
            skLineSegment(sketch, "E428", {"start": v(23.28, 203.81) * mm, "end": v(22.67, 205.15) * mm});
            skLineSegment(sketch, "E429", {"start": v(22.67, 205.15) * mm, "end": v(21.95, 206.46) * mm});
            skLineSegment(sketch, "E430", {"start": v(21.95, 206.46) * mm, "end": v(21.17, 207.73) * mm});
            skLineSegment(sketch, "E431", {"start": v(21.17, 207.73) * mm, "end": v(20.3, 208.94) * mm});
            skLineSegment(sketch, "E432", {"start": v(20.3, 208.94) * mm, "end": v(19.37, 210.1) * mm});
            skLineSegment(sketch, "E433", {"start": v(19.37, 210.1) * mm, "end": v(18.37, 211.22) * mm});
            skLineSegment(sketch, "E434", {"start": v(18.37, 211.22) * mm, "end": v(17.31, 212.26) * mm});
            skLineSegment(sketch, "E435", {"start": v(17.31, 212.26) * mm, "end": v(16.2, 213.23) * mm});
            skLineSegment(sketch, "E436", {"start": v(16.2, 213.23) * mm, "end": v(15.03, 214.16) * mm});
            skLineSegment(sketch, "E437", {"start": v(15.03, 214.16) * mm, "end": v(13.8, 215.01) * mm});
            skLineSegment(sketch, "E438", {"start": v(13.8, 215.01) * mm, "end": v(12.53, 215.77) * mm});
            skLineSegment(sketch, "E439", {"start": v(12.53, 215.77) * mm, "end": v(11.22, 216.47) * mm});
            skLineSegment(sketch, "E440", {"start": v(11.22, 216.47) * mm, "end": v(9.86, 217.09) * mm});
            skLineSegment(sketch, "E441", {"start": v(9.86, 217.09) * mm, "end": v(8.47, 217.61) * mm});
            skLineSegment(sketch, "E442", {"start": v(8.47, 217.61) * mm, "end": v(7.05, 218.08) * mm});
            skLineSegment(sketch, "E443", {"start": v(7.05, 218.08) * mm, "end": v(5.6, 218.44) * mm});
            skLineSegment(sketch, "E444", {"start": v(5.6, 218.44) * mm, "end": v(4.15, 218.74) * mm});
            skLineSegment(sketch, "E445", {"start": v(4.15, 218.74) * mm, "end": v(2.67, 218.93) * mm});
            skLineSegment(sketch, "E446", {"start": v(2.67, 218.93) * mm, "end": v(1.19, 219.05) * mm});
            skLineSegment(sketch, "E447", {"start": v(1.19, 219.05) * mm, "end": v(-0.3, 219.08) * mm});
            skLineSegment(sketch, "E448", {"start": v(-0.3, 219.08) * mm, "end": v(-1.78, 219.01) * mm});
            skLineSegment(sketch, "E449", {"start": v(-1.78, 219.01) * mm, "end": v(-3.26, 218.86) * mm});
            skLineSegment(sketch, "E450", {"start": v(-3.26, 218.86) * mm, "end": v(-4.74, 218.63) * mm});
            skLineSegment(sketch, "E451", {"start": v(-4.74, 218.63) * mm, "end": v(-6.18, 218.31) * mm});
            skLineSegment(sketch, "E452", {"start": v(-6.18, 218.31) * mm, "end": v(-7.62, 217.91) * mm});
            skLineSegment(sketch, "E453", {"start": v(-7.62, 217.91) * mm, "end": v(-9.04, 217.42) * mm});
            skLineSegment(sketch, "E454", {"start": v(-9.04, 217.42) * mm, "end": v(-10.4, 216.85) * mm});
            skLineSegment(sketch, "E455", {"start": v(-10.4, 216.85) * mm, "end": v(-11.75, 216.2) * mm});
            skLineSegment(sketch, "E456", {"start": v(-11.75, 216.2) * mm, "end": v(-13.04, 215.48) * mm});
            skLineSegment(sketch, "E457", {"start": v(-13.04, 215.48) * mm, "end": v(-14.29, 214.67) * mm});
            skLineSegment(sketch, "E458", {"start": v(-14.29, 214.67) * mm, "end": v(-15.5, 213.8) * mm});
            skLineSegment(sketch, "E459", {"start": v(-15.5, 213.8) * mm, "end": v(-16.66, 212.85) * mm});
            skLineSegment(sketch, "E460", {"start": v(-16.66, 212.85) * mm, "end": v(-17.74, 211.86) * mm});
            skLineSegment(sketch, "E461", {"start": v(-17.74, 211.86) * mm, "end": v(-18.77, 210.78) * mm});
            skLineSegment(sketch, "E462", {"start": v(-18.77, 210.78) * mm, "end": v(-19.75, 209.66) * mm});
            skLineSegment(sketch, "E463", {"start": v(-19.75, 209.66) * mm, "end": v(-20.66, 208.47) * mm});
            skLineSegment(sketch, "E464", {"start": v(-20.66, 208.47) * mm, "end": v(-21.48, 207.22) * mm});
            skLineSegment(sketch, "E465", {"start": v(-21.48, 207.22) * mm, "end": v(-22.25, 205.95) * mm});
            skLineSegment(sketch, "E466", {"start": v(-22.25, 205.95) * mm, "end": v(-22.92, 204.62) * mm});
            skLineSegment(sketch, "E467", {"start": v(-22.92, 204.62) * mm, "end": v(-23.52, 203.26) * mm});
            skLineSegment(sketch, "E468", {"start": v(-23.52, 203.26) * mm, "end": v(-24.05, 201.87) * mm});
            skLineSegment(sketch, "E469", {"start": v(-24.05, 201.87) * mm, "end": v(-24.49, 200.45) * mm});
            skLineSegment(sketch, "E470", {"start": v(-24.49, 200.45) * mm, "end": v(-24.83, 198.99) * mm});
            skLineSegment(sketch, "E471", {"start": v(-24.83, 198.99) * mm, "end": v(-25.1, 197.53) * mm});
            skLineSegment(sketch, "E472", {"start": v(-25.1, 197.53) * mm, "end": v(-25.3, 196.05) * mm});
            skLineSegment(sketch, "E473", {"start": v(-25.3, 196.05) * mm, "end": v(-25.38, 194.56) * mm});
            skLineSegment(sketch, "E474", {"start": v(-25.38, 194.56) * mm, "end": v(-25.4, 193.08) * mm});
            skLineSegment(sketch, "E475", {"start": v(-25.4, 193.08) * mm, "end": v(-25.32, 191.6) * mm});
            skLineSegment(sketch, "E476", {"start": v(-25.32, 191.6) * mm, "end": v(-25.15, 190.12) * mm});
            skLineSegment(sketch, "E477", {"start": v(-25.15, 190.12) * mm, "end": v(-24.9, 188.66) * mm});
            skLineSegment(sketch, "E478", {"start": v(-24.9, 188.66) * mm, "end": v(-24.55, 187.2) * mm});
            skLineSegment(sketch, "E479", {"start": v(-24.55, 187.2) * mm, "end": v(-24.13, 185.78) * mm});
            skLineSegment(sketch, "E480", {"start": v(-24.13, 185.78) * mm, "end": v(-23.64, 184.36) * mm});
            skLineSegment(sketch, "E481", {"start": v(-23.64, 184.36) * mm, "end": v(-23.05, 183) * mm});
            skLineSegment(sketch, "E482", {"start": v(-23.05, 183) * mm, "end": v(-22.37, 181.67) * mm});
            skLineSegment(sketch, "E483", {"start": v(-22.37, 181.67) * mm, "end": v(-21.63, 180.38) * mm});
            skLineSegment(sketch, "E484", {"start": v(-21.63, 180.38) * mm, "end": v(-20.83, 179.13) * mm});
            skLineSegment(sketch, "E485", {"start": v(-20.83, 179.13) * mm, "end": v(-19.94, 177.95) * mm});
            skLineSegment(sketch, "E486", {"start": v(-19.94, 177.95) * mm, "end": v(-18.99, 176.8) * mm});
            skLineSegment(sketch, "E487", {"start": v(-18.99, 176.8) * mm, "end": v(-17.97, 175.73) * mm});
            skLineSegment(sketch, "E488", {"start": v(-25.4, -206.14) * mm, "end": v(-25.4, -212.73) * mm});
            skLineSegment(sketch, "E489", {"start": v(-25.4, -164.87) * mm, "end": v(-25.4, -180.49) * mm});
            skLineSegment(sketch, "E490", {"start": v(-25.4, -123.6) * mm, "end": v(-25.4, -139.21) * mm});
            skLineSegment(sketch, "E491", {"start": v(-25.4, -82.32) * mm, "end": v(-25.4, -97.94) * mm});
            skLineSegment(sketch, "E492", {"start": v(-25.4, -41.04) * mm, "end": v(-25.4, -56.66) * mm});
            skLineSegment(sketch, "E493", {"start": v(-25.4, 0.23) * mm, "end": v(-25.4, -15.39) * mm});
            skLineSegment(sketch, "E494", {"start": v(-25.4, 41.5) * mm, "end": v(-25.4, 25.89) * mm});
            skLineSegment(sketch, "E495", {"start": v(-25.4, 82.78) * mm, "end": v(-25.4, 67.16) * mm});
            skLineSegment(sketch, "E496", {"start": v(-25.4, 123.1) * mm, "end": v(-25.4, 108.44) * mm});
            skLineSegment(sketch, "E497", {"start": v(0, 144.19) * mm, "end": v(0, 152.5) * mm});
            skLineSegment(sketch, "E498", {"start": v(0, 152.5) * mm, "end": v(-0.04, 153.5) * mm});
            skLineSegment(sketch, "E499", {"start": v(-0.04, 153.5) * mm, "end": v(-0.15, 154.47) * mm});
            skLineSegment(sketch, "E500", {"start": v(-0.15, 154.47) * mm, "end": v(-0.36, 155.47) * mm});
            skLineSegment(sketch, "E501", {"start": v(-0.36, 155.47) * mm, "end": v(-0.61, 156.42) * mm});
            skLineSegment(sketch, "E502", {"start": v(-0.61, 156.42) * mm, "end": v(-0.97, 157.35) * mm});
            skLineSegment(sketch, "E503", {"start": v(-0.97, 157.35) * mm, "end": v(-1.38, 158.26) * mm});
            skLineSegment(sketch, "E504", {"start": v(-1.38, 158.26) * mm, "end": v(-1.86, 159.13) * mm});
            skLineSegment(sketch, "E505", {"start": v(-1.86, 159.13) * mm, "end": v(-2.43, 159.96) * mm});
            skLineSegment(sketch, "E506", {"start": v(-2.43, 159.96) * mm, "end": v(-3.05, 160.74) * mm});
            skLineSegment(sketch, "E507", {"start": v(-3.05, 160.74) * mm, "end": v(-3.73, 161.48) * mm});
            skLineSegment(sketch, "E508", {"start": v(-17.97, 175.73) * mm, "end": v(-3.73, 161.48) * mm});
            skSolve(sketch);
        }
        {
            var Q0;
            Q0 = qSketchRegion(id + "F0", true);
            extrude(context, id + "F1", {"entities" : qUnion([Q0]), "depth" : 12.7 * mm, "offsetDistance" : 25.4 * mm});
        }
    });
